# Revit family: Faucet_Utility-Exposed-Wall_Mounted-American_Standard-Yoke-8354112_Series
name_source: partatom
category: Plumbing Fixtures
units: mm (PartAtom-declared; Revit-internal decimal feet)

## family parameters
Always vertical = Yes
Cut with Voids When Loaded = No
OmniClass Number = 23.45.55.17
OmniClass Title = Mixing Faucets
Part Type = Normal
Room Calculation Point = No
Round Connector Dimension = Use Diameter
Shared = Yes
Work Plane-Based = Yes

## types (2) — shared parameters
ADA Compliant = Yes
Assembly Code = D2020
CW Connection = Yes
CWFU = 1.5
Cold Water Connection Diameter = 1/2"
Default Elevation = 36"
Description = Top Brace Wall-Mount Service Sink Faucet With 6-Inch Vacuum Breaker Spout and Offset Shanks
HW Connection = No
HWFU = 1.5
Height = 2 1/2"
Hot Water Connection Diameter = 1/2"
Installation Instruction Link = https://americanstandard.box.com
Length = 12 1/2"
Manufacturer = American Standard
Product Documentation Link = https://americanstandard.box.com
Product Page URL = https://www.americanstandard-us.com
Revised Date = 02/20/2023
Specification = Exposed Yoke Wall-Mount Utility Faucet Top brace. 6" cast brass spout with vacuum breaker. Ceramic disc valves. Integral supply stops. Offset shanks with integral check valves. Vandal-resistant metal lever handles. Bucket hook. 3/4" threaded hose end. 1/2" NPT female inlets. Adjustable centers-to-centers: 6"-10" (152mm - 254mm).
URL = http://www.americanstandard-us.com
Vent Connection = No
Waste Connection = Yes
Width = 7 1/4"
zero-valued in all types: Cost, WFU

## per-type parameters (varying)
| type | Finish | Material |
| 8354112.004 | Brass-American Standard-004-RoughChrome | Brass-American Standard-004-RoughChrome |
| 8354112.002 | Brass-American Standard-002-Polished Chrome | Brass-American Standard-002-Polished Chrome |

note: column(s) folded — value = type name in every type: Model
